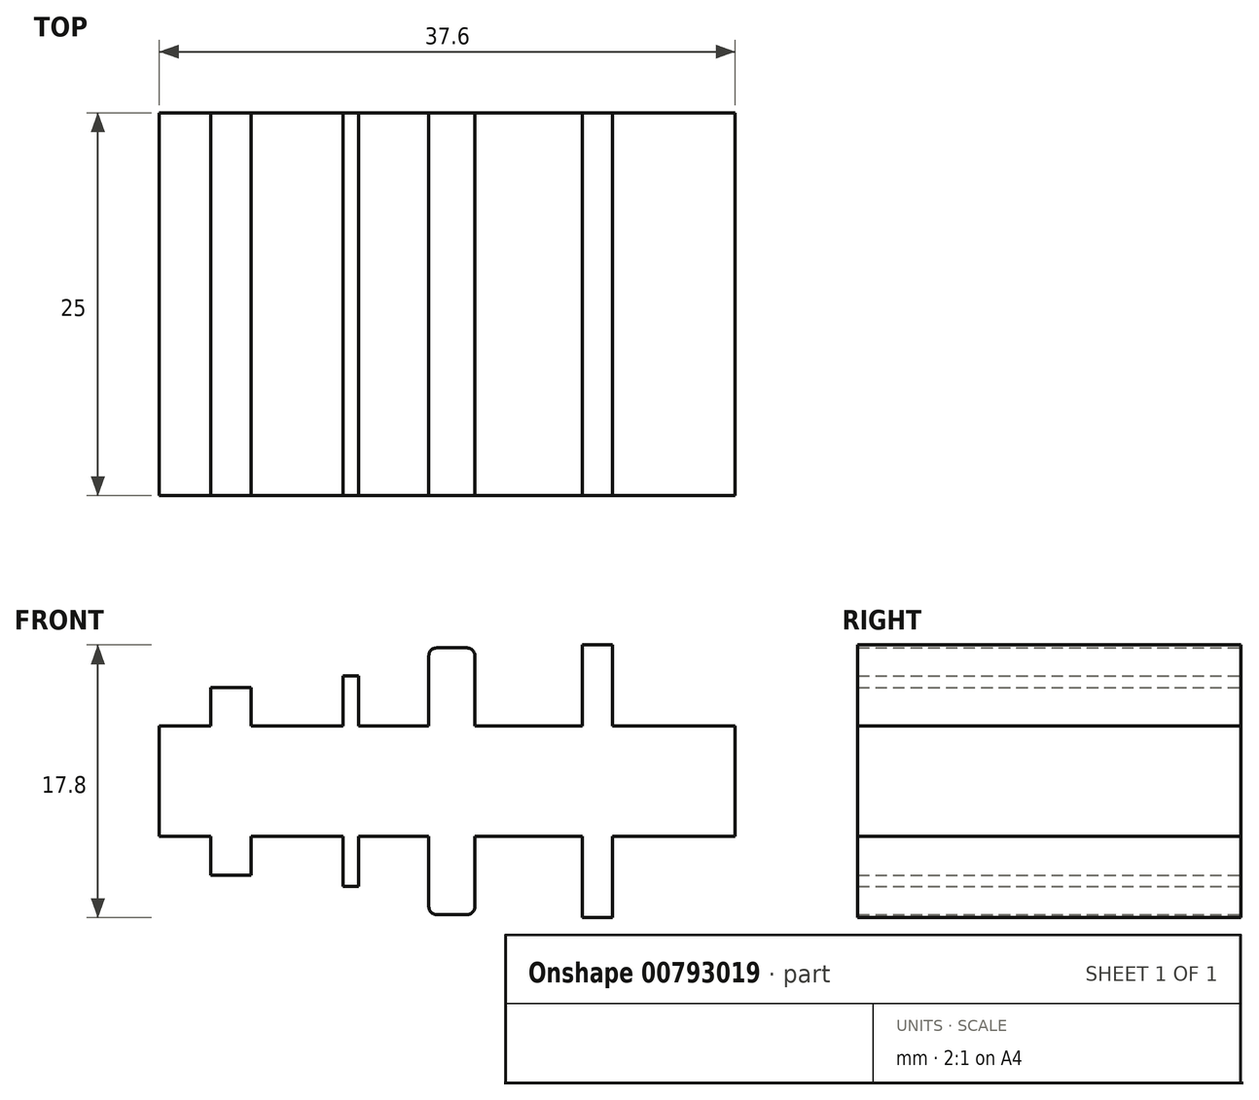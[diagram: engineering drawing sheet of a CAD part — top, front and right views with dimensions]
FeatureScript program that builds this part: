
annotation { "Feature Type Name" : "Feature", "Feature Type Description" : "" }
export const myFeature = defineFeature(function(context is Context, id is Id, definition is map)
    precondition{}
    {
        {
            var Q0;
            Q0=qCreatedBy(makeId("Front.planeOp"),FACE);
            var sketch = newSketch(context, id + "F0", { "sketchPlane" : qUnion([Q0])});
            skLineSegment(sketch, "E0.bottom", {"start": v(18.8, -3.6) * mm, "end": v(-18.8, -3.6) * mm});
            skLineSegment(sketch, "E0.top", {"start": v(18.8, 3.6) * mm, "end": v(-18.8, 3.6) * mm});
            skLineSegment(sketch, "E0.left", {"start": v(18.8, -3.6) * mm, "end": v(18.8, 3.6) * mm});
            skLineSegment(sketch, "E0.right", {"start": v(-18.8, -3.6) * mm, "end": v(-18.8, 3.6) * mm});
            skPoint(sketch, "E0.middle", {"position": v(0, 0) * mm});
            skLineSegment(sketch, "E1", {"start": v(-15.45, 3.6) * mm, "end": v(-15.45, 6.12) * mm});
            skLineSegment(sketch, "E2", {"start": v(-15.45, 6.12) * mm, "end": v(-12.8, 6.12) * mm});
            skLineSegment(sketch, "E3", {"start": v(-12.8, 6.12) * mm, "end": v(-12.8, 3.6) * mm});
            skLineSegment(sketch, "E4", {"start": v(-6.8, 3.6) * mm, "end": v(-6.8, 6.88) * mm});
            skLineSegment(sketch, "E5", {"start": v(-6.8, 6.88) * mm, "end": v(-5.8, 6.88) * mm});
            skLineSegment(sketch, "E6", {"start": v(-5.8, 6.88) * mm, "end": v(-5.8, 3.6) * mm});
            skLineSegment(sketch, "E7", {"start": v(-1.2, 3.6) * mm, "end": v(-1.2, 8.2) * mm});
            skLineSegment(sketch, "E8", {"start": v(-0.7, 8.7) * mm, "end": v(1.3, 8.7) * mm});
            skLineSegment(sketch, "E9", {"start": v(1.8, 8.2) * mm, "end": v(1.8, 3.6) * mm});
            skLineSegment(sketch, "E10", {"start": v(8.8, 3.6) * mm, "end": v(8.8, 8.9) * mm});
            skLineSegment(sketch, "E11", {"start": v(8.8, 8.9) * mm, "end": v(10.8, 8.9) * mm});
            skLineSegment(sketch, "E12", {"start": v(10.8, 8.9) * mm, "end": v(10.8, 3.6) * mm});
            skPoint(sketch, "E13.visualSharp", {"position": v(-1.2, 8.7) * mm});
            skArc(sketch, "E13.filletArc", {"start": v(-0.7, 8.7) * mm, "mid": v(-1.05, 8.56) * mm, "end": v(-1.2, 8.2) * mm});
            skPoint(sketch, "E14.visualSharp", {"position": v(1.8, 8.7) * mm});
            skArc(sketch, "E14.filletArc", {"start": v(1.8, 8.2) * mm, "mid": v(1.65, 8.56) * mm, "end": v(1.3, 8.7) * mm});
            skLineSegment(sketch, "E15.MirrorCS", {"start": v(-15.45, -3.6) * mm, "end": v(-15.45, -6.12) * mm});
            skLineSegment(sketch, "E16.MirrorCS", {"start": v(-15.45, -6.12) * mm, "end": v(-12.8, -6.12) * mm});
            skLineSegment(sketch, "E17.MirrorCS", {"start": v(-12.8, -6.12) * mm, "end": v(-12.8, -3.6) * mm});
            skLineSegment(sketch, "E18.MirrorCS", {"start": v(-6.8, -3.6) * mm, "end": v(-6.8, -6.88) * mm});
            skLineSegment(sketch, "E19.MirrorCS", {"start": v(-5.8, -6.88) * mm, "end": v(-5.8, -3.6) * mm});
            skLineSegment(sketch, "E20.MirrorCS", {"start": v(-6.8, -6.88) * mm, "end": v(-5.8, -6.88) * mm});
            skLineSegment(sketch, "E21.MirrorCS", {"start": v(-1.2, -3.6) * mm, "end": v(-1.2, -8.2) * mm});
            skLineSegment(sketch, "E22.MirrorCS", {"start": v(-0.7, -8.7) * mm, "end": v(1.3, -8.7) * mm});
            skLineSegment(sketch, "E23.MirrorCS", {"start": v(1.8, -8.2) * mm, "end": v(1.8, -3.6) * mm});
            skArc(sketch, "E24.MirrorCS", {"start": v(1.8, -8.2) * mm, "mid": v(1.65, -8.56) * mm, "end": v(1.3, -8.7) * mm});
            skArc(sketch, "E25.MirrorCS", {"start": v(-0.7, -8.7) * mm, "mid": v(-1.05, -8.56) * mm, "end": v(-1.2, -8.2) * mm});
            skLineSegment(sketch, "E26.MirrorCS", {"start": v(8.8, -3.6) * mm, "end": v(8.8, -8.9) * mm});
            skLineSegment(sketch, "E27.MirrorCS", {"start": v(8.8, -8.9) * mm, "end": v(10.8, -8.9) * mm});
            skLineSegment(sketch, "E28.MirrorCS", {"start": v(10.8, -8.9) * mm, "end": v(10.8, -3.6) * mm});
            skSolve(sketch);
        }
        {
            var Q0;
            Q0 = qSketchRegion(id + "F0", true);
            extrude(context, id + "F1", {"entities" : qUnion([Q0]), "depth" : 25 * mm, "offsetDistance" : 25 * mm});
        }
        {
            var Q0;
            Q0=makeQuery(id+"F1.opExtrude","SWEPT_FACE",FACE,{"disambiguationData":[OSD([sQuery(id+"F0.wireOp",EDGE,"E0.right")])]});
            var sketch = newSketch(context, id + "F2", { "sketchPlane" : qUnion([Q0])});
            skCircle(sketch, "E29", {"center": v(12.26, 0) * mm, "radius": 3.6 * mm});
            skCircle(sketch, "E30", {"center": v(12.26, 0) * mm, "radius": 2.25 * mm});
            skSolve(sketch);
        }
        {
            var Q0;
            Q0 = qSketchRegion(id + "F2", true);
            extrude(context, id + "F3", {"entities" : qUnion([Q0]), "operationType" : NewBodyOperationType.ADD, "oppositeDirection" : true, "depth" : 25 * mm, "offsetDistance" : 25 * mm});
        }
    });
